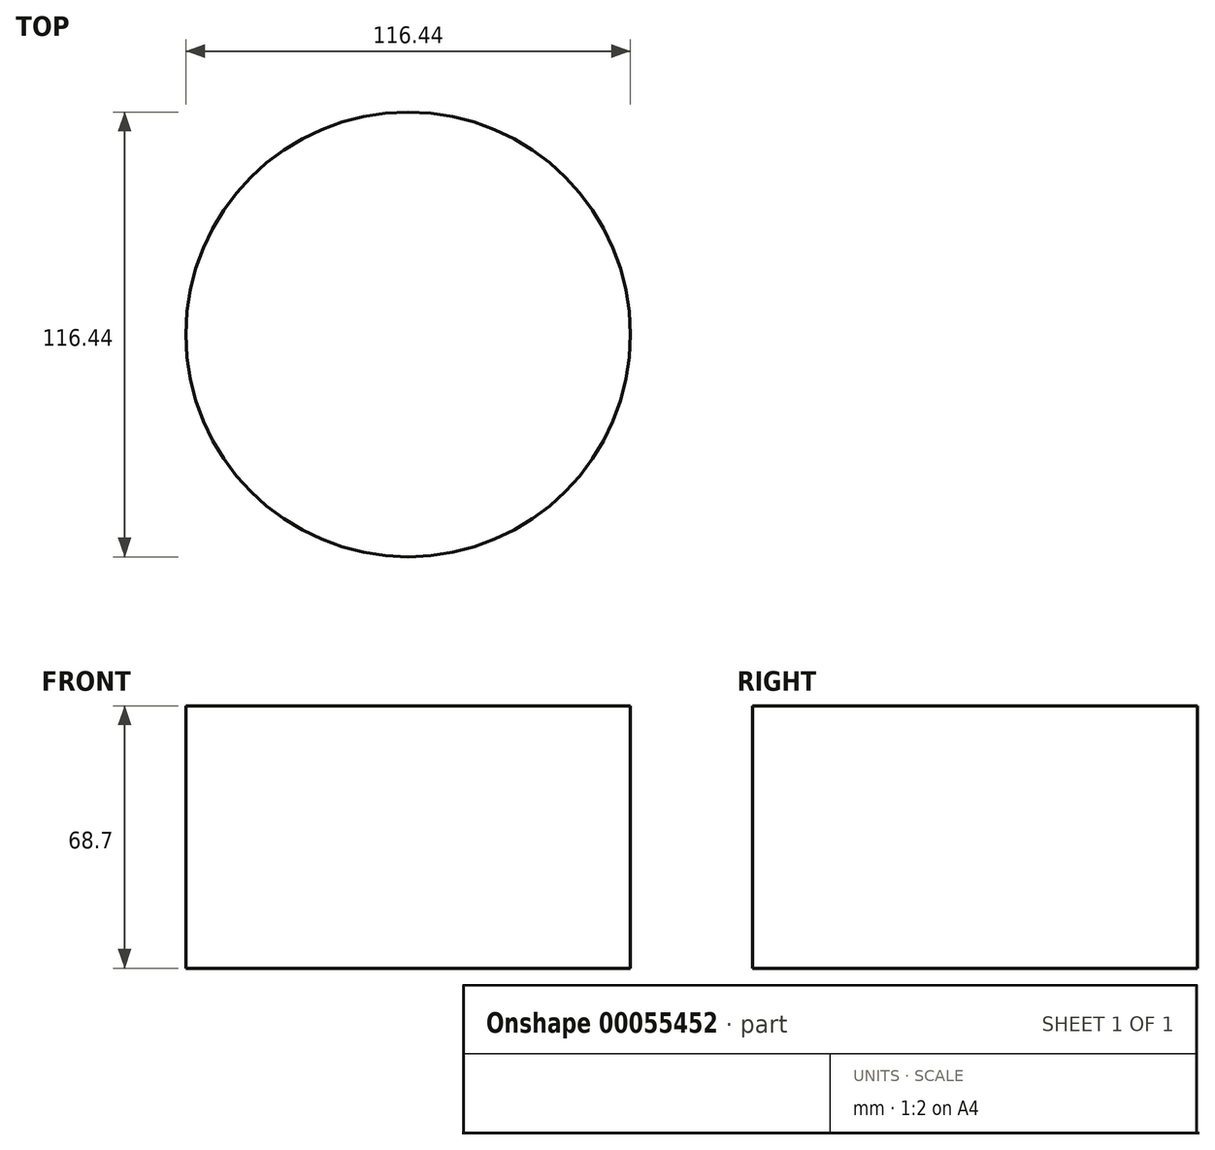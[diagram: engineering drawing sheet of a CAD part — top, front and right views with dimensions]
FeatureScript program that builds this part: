
annotation { "Feature Type Name" : "Feature", "Feature Type Description" : "" }
export const myFeature = defineFeature(function(context is Context, id is Id, definition is map)
    precondition{}
    {
        {
            var Q0;
            Q0=qCreatedBy(makeId("Top.planeOp"),FACE);
            var sketch = newSketch(context, id + "F0", { "sketchPlane" : qUnion([Q0])});
            skCircle(sketch, "E0", {"center": v(0, 0) * mm, "radius": 58.22 * mm});
            skSolve(sketch);
        }
        {
            var Q0;
            Q0=makeQuery(id+"F0.imprint","IMPRINT",FACE,{"disambiguationData":[TD([[makeQuery(id+"F0.imprint","IMPRINT",EDGE,{"derivedFrom":sQuery(id+"F0.wireOp",EDGE,"E0")}),1.0]])]});
            extrude(context, id + "F1", {"entities" : qUnion([Q0]), "oppositeDirection" : true, "depth" : 68.7 * mm});
        }
    });
